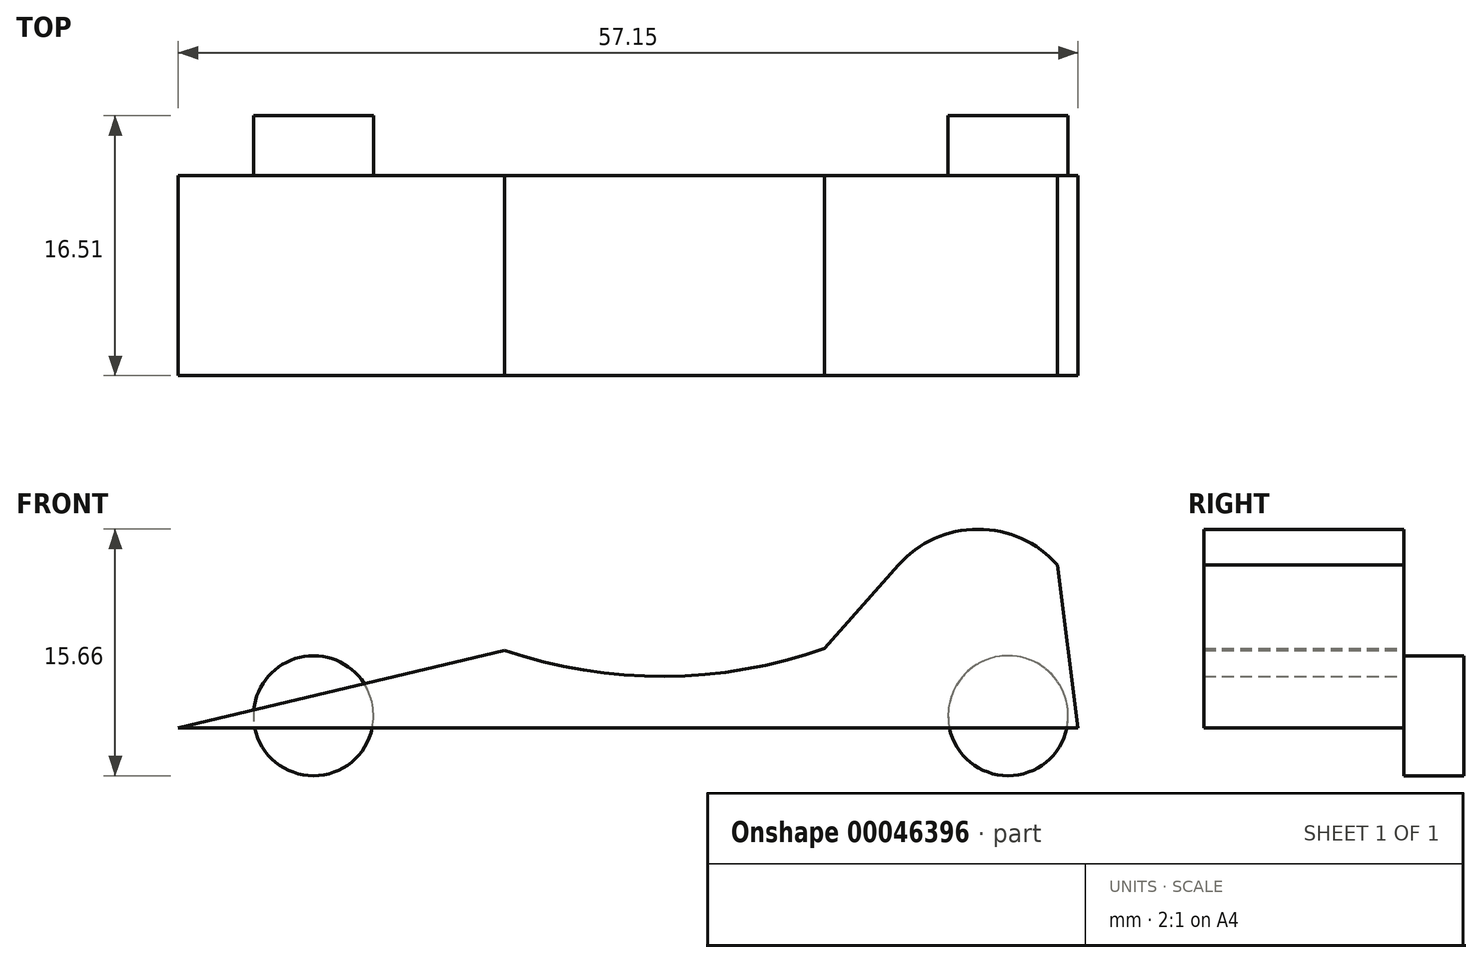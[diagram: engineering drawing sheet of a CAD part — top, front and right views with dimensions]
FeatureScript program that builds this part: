
annotation { "Feature Type Name" : "Feature", "Feature Type Description" : "" }
export const myFeature = defineFeature(function(context is Context, id is Id, definition is map)
    precondition{}
    {
        {
            var Q0;
            Q0=qCreatedBy(makeId("Front.planeOp"),FACE);
            var sketch = newSketch(context, id + "F0", { "sketchPlane" : qUnion([Q0])});
            skLineSegment(sketch, "E0", {"start": v(-26.62, 0) * mm, "end": v(30.53, 0) * mm});
            skLineSegment(sketch, "E1", {"start": v(14.43, 5.03) * mm, "end": v(19.13, 10.33) * mm});
            skLineSegment(sketch, "E2", {"start": v(29.22, 10.33) * mm, "end": v(30.53, 0) * mm});
            skArc(sketch, "E3", {"start": v(29.22, 10.33) * mm, "mid": v(24.18, 12.6) * mm, "end": v(19.13, 10.33) * mm});
            skLineSegment(sketch, "E4", {"start": v(-26.62, 0) * mm, "end": v(-5.9, 4.92) * mm});
            skArc(sketch, "E5", {"start": v(-5.9, 4.92) * mm, "mid": v(4.27, 3.27) * mm, "end": v(14.43, 5.03) * mm});
            skSolve(sketch);
        }
        {
            var Q0;
            Q0 = qSketchRegion(id + "F0", true);
            extrude(context, id + "F1", {"entities" : qUnion([Q0]), "depth" : 12.7 * mm});
        }
        {
            var Q0;
            Q0=makeQuery(id+"F0.imprint","IMPRINT",FACE,{"disambiguationData":[TD([[makeQuery(id+"F0.imprint","IMPRINT",EDGE,{"derivedFrom":sQuery(id+"F0.wireOp",EDGE,"E0")}),1.0]])]});
            var sketch = newSketch(context, id + "F2", { "sketchPlane" : qUnion([Q0])});
            skCircle(sketch, "E6", {"center": v(-18.03, 0.76) * mm, "radius": 3.81 * mm});
            skCircle(sketch, "E7", {"center": v(26.1, 0.76) * mm, "radius": 3.81 * mm});
            skSolve(sketch);
        }
        {
            var Q0;
            Q0 = qSketchRegion(id + "F2", true);
            extrude(context, id + "F3", {"entities" : qUnion([Q0]), "operationType" : NewBodyOperationType.ADD, "oppositeDirection" : true, "depth" : 3.8 * mm});
        }
    });
